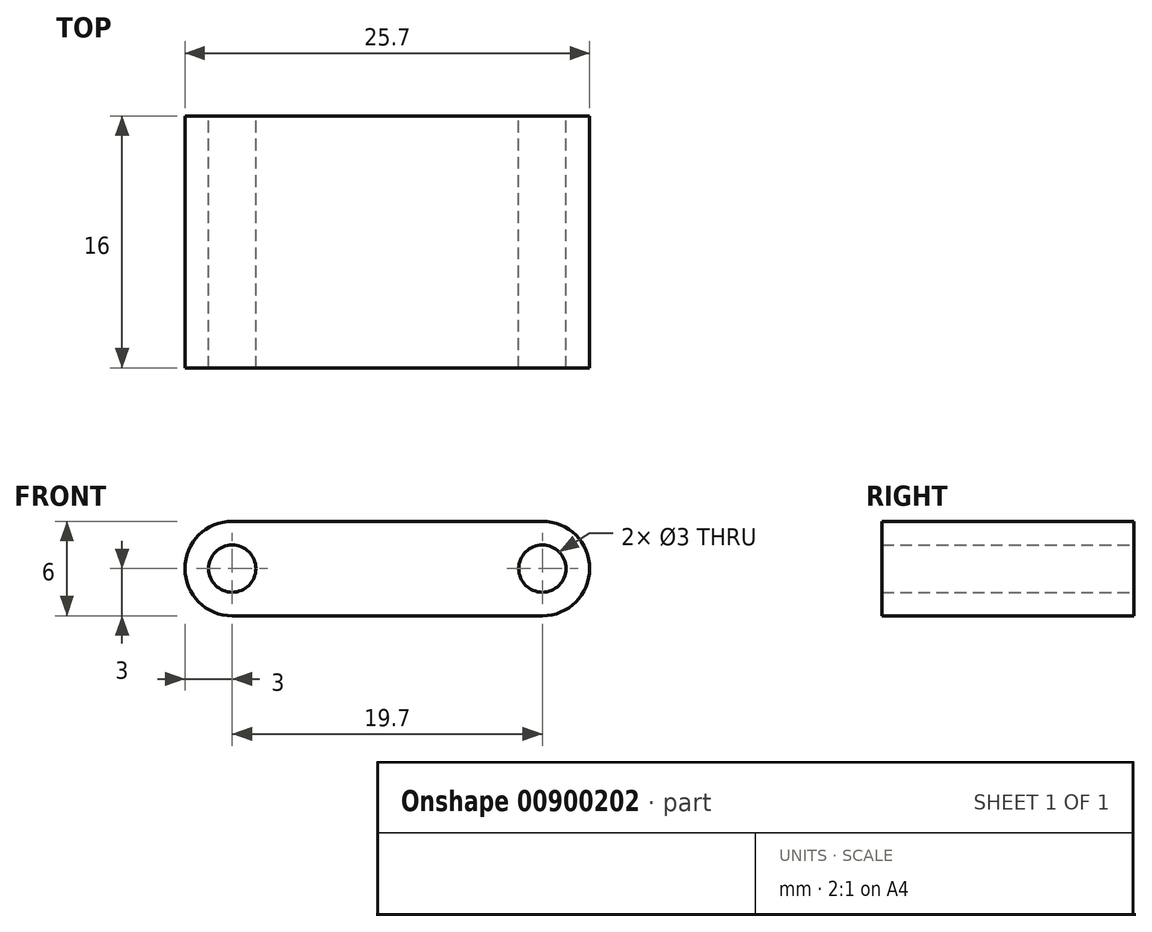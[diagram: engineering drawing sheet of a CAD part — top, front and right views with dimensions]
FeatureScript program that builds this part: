
annotation { "Feature Type Name" : "Feature", "Feature Type Description" : "" }
export const myFeature = defineFeature(function(context is Context, id is Id, definition is map)
    precondition{}
    {
        {
            var Q0;
            Q0=qCreatedBy(makeId("Front.planeOp"),FACE);
            var sketch = newSketch(context, id + "F0", { "sketchPlane" : qUnion([Q0])});
            skLineSegment(sketch, "E0", {"start": v(-9.85, 0) * mm, "end": v(9.85, 0) * mm});
            skCircle(sketch, "E1", {"center": v(9.85, 0) * mm, "radius": 1.5 * mm});
            skCircle(sketch, "E2", {"center": v(-9.85, 0) * mm, "radius": 1.5 * mm});
            skPoint(sketch, "E3.visualSharp", {"position": v(-66.12, -69.63) * mm});
            skArc(sketch, "E3.filletArc", {"start": v(-51.94, -37.1) * mm, "mid": v(-52.74, -38.3) * mm, "end": v(-51.92, -39.49) * mm});
            skArc(sketch, "E4", {"start": v(-9.85, 3) * mm, "mid": v(-12.85, 0) * mm, "end": v(-9.85, -3) * mm});
            skArc(sketch, "E5", {"start": v(9.85, -3) * mm, "mid": v(12.85, 0) * mm, "end": v(9.85, 3) * mm});
            skLineSegment(sketch, "E6", {"start": v(9.85, 3) * mm, "end": v(-9.85, 3) * mm});
            skLineSegment(sketch, "E7", {"start": v(-9.85, -3) * mm, "end": v(9.85, -3) * mm});
            skSolve(sketch);
        }
        {
            var Q0;
            Q0 = qSketchRegion(id + "F0", true);
            extrude(context, id + "F1", {"entities" : qUnion([Q0]), "endBound" : BoundingType.SYMMETRIC, "depth" : 16 * mm, "offsetDistance" : 25.4 * mm});
        }
    });
